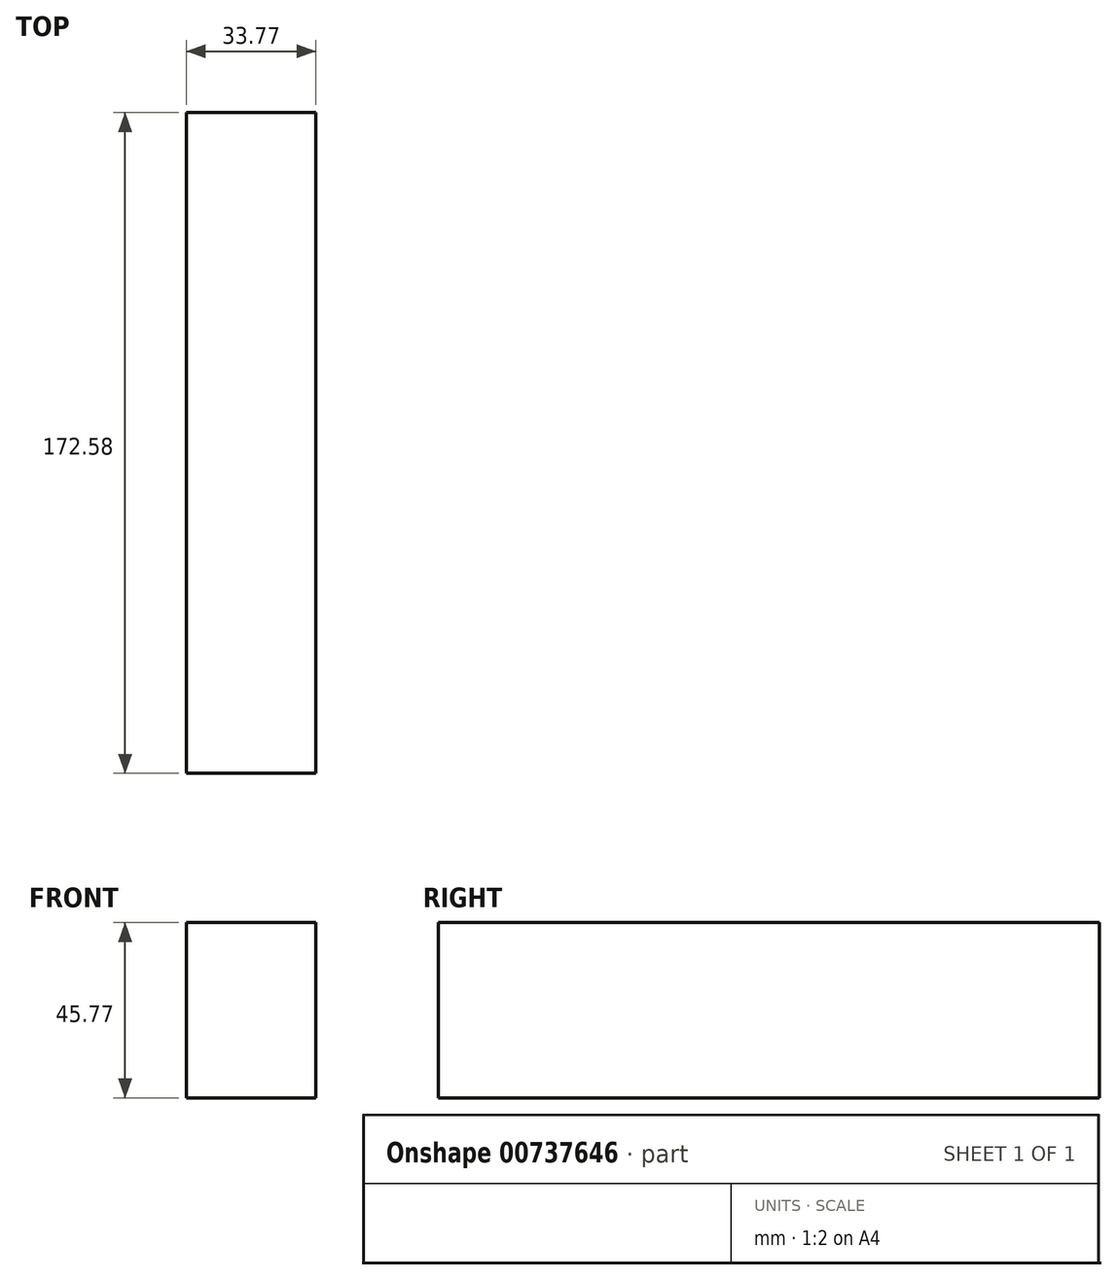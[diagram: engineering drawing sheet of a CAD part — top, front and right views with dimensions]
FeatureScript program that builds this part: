
annotation { "Feature Type Name" : "Feature", "Feature Type Description" : "" }
export const myFeature = defineFeature(function(context is Context, id is Id, definition is map)
    precondition{}
    {
        {
            var Q0;
            Q0=qCreatedBy(makeId("Top.planeOp"),FACE);
            var sketch = newSketch(context, id + "F0", { "sketchPlane" : qUnion([Q0])});
            skLineSegment(sketch, "E0.bottom", {"start": v(23.5, -27.62) * mm, "end": v(57.26, -27.62) * mm});
            skLineSegment(sketch, "E0.top", {"start": v(23.5, 144.96) * mm, "end": v(57.26, 144.96) * mm});
            skLineSegment(sketch, "E0.left", {"start": v(23.5, -27.62) * mm, "end": v(23.5, 144.96) * mm});
            skLineSegment(sketch, "E0.right", {"start": v(57.26, -27.62) * mm, "end": v(57.26, 144.96) * mm});
            skSolve(sketch);
        }
        {
            var Q0;
            Q0 = qSketchRegion(id + "F0", true);
            var sketch = newSketch(context, id + "F1", { "sketchPlane" : qUnion([Q0])});
            skSolve(sketch);
        }
        {
            var Q0;
            Q0=makeQuery(id+"F1.imprint","IMPRINT",FACE,{"disambiguationData":[TD([[makeQuery(id+"F1.imprint","IMPRINT",EDGE,{"derivedFrom":makeQuery(id+"F0.imprint","IMPRINT",EDGE,{"derivedFrom":sQuery(id+"F0.wireOp",EDGE,"E0.bottom")})}),1.0]])]});
            extrude(context, id + "F2", {"entities" : qUnion([Q0]), "depth" : 45.77 * mm, "offsetDistance" : 25.4 * mm});
        }
    });
